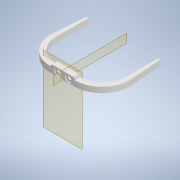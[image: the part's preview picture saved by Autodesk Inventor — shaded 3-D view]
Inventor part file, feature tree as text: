
AUTODESK INVENTOR PART (.ipt)
format: ipt  version: 2020 (Build 240168000, 168)  size: 169,472 bytes
history: native  units: mm
features: sketch x4, extrude x3, other x3, plane x2, hole x1, draft x1, mirror x1, reference x1
ambient origin geometry x8: Origin, YZ Plane, XZ Plane, XY Plane, X Axis, Y Axis, Z Axis, Center Point
bodies: Solid1 (feature_tree)
feature tree (16):
  plane  "Work Plane1"
  extrude  "Extrusion1"  Depth=1.5mm
  hole  "Hole1"  [1 undecoded]
  extrude  "Extrusion2"  Depth=50.0mm
  draft  "FaceDraft1"
  sketch  "Sketch5"  dims[d13=0.872665mm d14=50.0mm d15=5.0mm d16=0.0mm d17=0.5mm d18=0.872665mm]
  plane  "Work Plane2"
  extrude  "Extrusion3"  Depth=5.0mm TaperAngle=0.0deg
  mirror  "Mirror1"
  sketch  "Sketch1"  dims[d0=5.0mm d1=0.0mm]
  reference  "Reference1"
  sketch  "Sketch2"  dims[d2=3.0mm d3=6.0mm d4=6.5mm d5=1.0mm d6=90.0deg d7=8.0mm d8=20.594885mm d9=1.5mm]
  sketch  "Sketch4"  dims[d10=2.0mm d11=0.0mm d12=0.0mm]
  parser-record x1  (decoder bookkeeping rows leaked as tree rows — omitted from the tree; the rows remain in map.json)
  other  "motorized2.iam"
  other  "servo_bracket:1"
note: 1 required parameter value undecoded (feature->parameter linkage not recoverable at this tier; creation-order binding heuristic only, values carry confidence <= 0.55)
note: 1 file-system path scrubbed to <path> (originals preserved in map.json)
